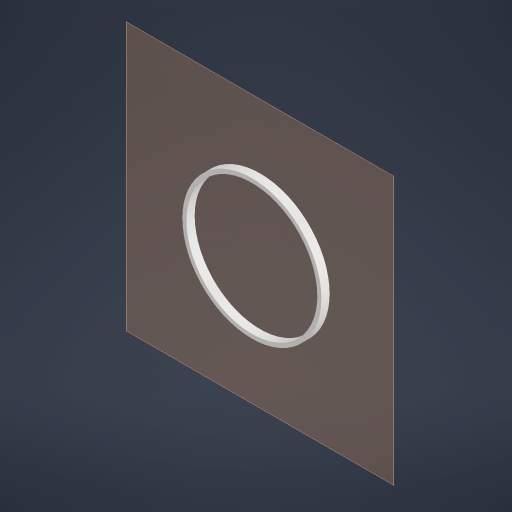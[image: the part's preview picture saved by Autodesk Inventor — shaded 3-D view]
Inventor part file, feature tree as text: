
AUTODESK INVENTOR PART (.ipt)
format: ipt  version: 2023.1 (Build 271208000, 208)  size: 177,664 bytes
history: native  units: mm
features: other x3, plane x1, extrude x1, sketch x1
ambient origin geometry x8: Origin, YZ Plane, XZ Plane, XY Plane, X Axis, Y Axis, Z Axis, Center Point
bodies: Solid1 (feature_tree)
feature tree (6):
  plane  "Work Plane1"
  extrude  "Extrusion1"  Depth=10.0mm
  sketch  "Sketch1"  dims[d0=159.155mm d1=5.0mm d2=10.0mm d3=0.0mm]
  parser-record x1  (decoder bookkeeping rows leaked as tree rows — omitted from the tree; the rows remain in map.json)
  other  "Beau4tClock.iam"
  other  "Clock:1"
note: 1 file-system path scrubbed to <path> (originals preserved in map.json)
